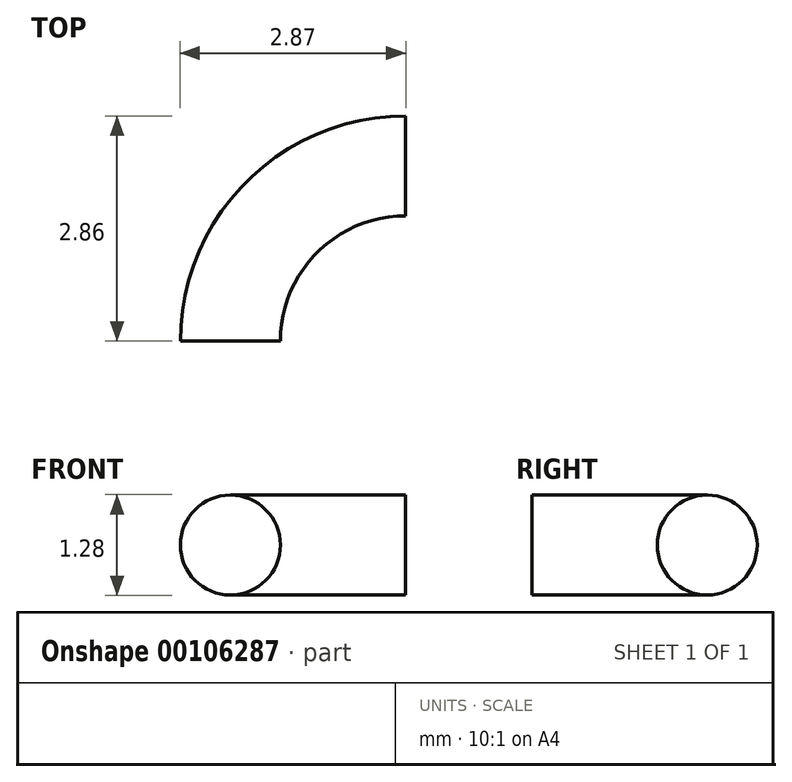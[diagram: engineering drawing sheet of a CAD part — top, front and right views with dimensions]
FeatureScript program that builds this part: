
annotation { "Feature Type Name" : "Feature", "Feature Type Description" : "" }
export const myFeature = defineFeature(function(context is Context, id is Id, definition is map)
    precondition{}
    {
        {
            var Q0;
            Q0=qCreatedBy(makeId("Front.planeOp"),FACE);
            var sketch = newSketch(context, id + "F0", { "sketchPlane" : qUnion([Q0])});
            skCircle(sketch, "E0", {"center": v(0, 0) * mm, "radius": 0.64 * mm});
            skSolve(sketch);
        }
        {
            var Q0;
            Q0=qCreatedBy(makeId("Top.planeOp"),FACE);
            var sketch = newSketch(context, id + "F1", { "sketchPlane" : qUnion([Q0])});
            skArc(sketch, "E1", {"start": v(0, 0) * mm, "mid": v(0.65, 1.57) * mm, "end": v(2.23, 2.23) * mm});
            skSolve(sketch);
        }
        {
            var Q0;
            Q0 = qSketchRegion(id + "F0", true);
            var Q1;
            Q1 = qConstructionFilter(qBodyType(qCreatedBy(id + "F1" ,EDGE), BodyType.WIRE), ConstructionObject.NO);
            sweep(context, id + "F2", {"profiles" : qUnion([Q0]), "path" : qUnion([Q1])});
        }
    });
